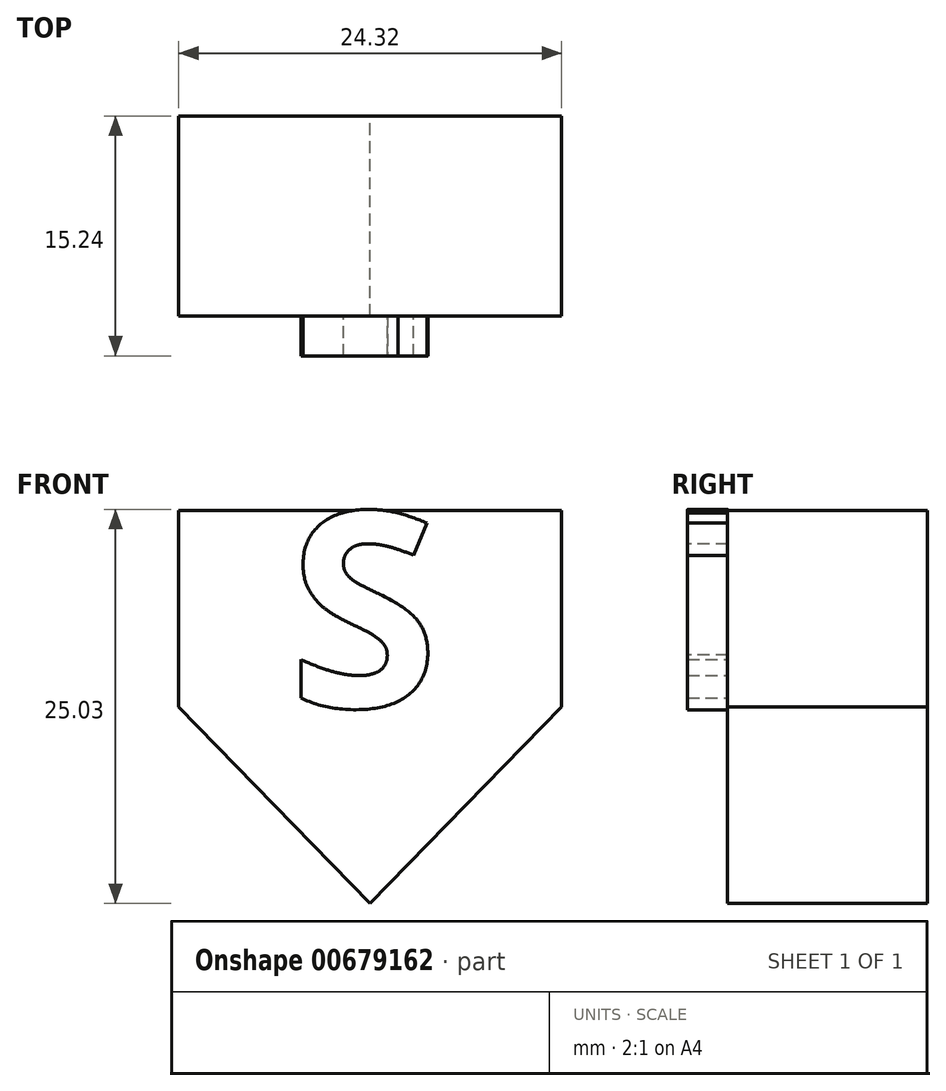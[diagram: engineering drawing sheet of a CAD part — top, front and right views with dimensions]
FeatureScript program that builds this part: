
annotation { "Feature Type Name" : "Feature", "Feature Type Description" : "" }
export const myFeature = defineFeature(function(context is Context, id is Id, definition is map)
    precondition{}
    {
        {
            var Q0;
            Q0=qCreatedBy(makeId("Front.planeOp"),FACE);
            var sketch = newSketch(context, id + "F0", { "sketchPlane" : qUnion([Q0])});
            skLineSegment(sketch, "E0.bottom", {"start": v(12.16, 12.48) * mm, "end": v(-12.16, 12.48) * mm});
            skLineSegment(sketch, "E0.top", {"start": v(12.16, -12.48) * mm, "end": v(-12.16, -12.48) * mm});
            skLineSegment(sketch, "E0.left", {"start": v(12.16, 12.48) * mm, "end": v(12.16, -12.48) * mm});
            skLineSegment(sketch, "E0.right", {"start": v(-12.16, 12.48) * mm, "end": v(-12.16, -12.48) * mm});
            skPoint(sketch, "E0.middle", {"position": v(0, 0) * mm});
            skLineSegment(sketch, "E1", {"start": v(-12.16, 0) * mm, "end": v(0, -12.48) * mm});
            skLineSegment(sketch, "E2", {"start": v(12.16, 0) * mm, "end": v(0, -12.48) * mm});
            skSolve(sketch);
        }
        {
            var Q0;
            {var subQ2=sQuery(id+"F0.wireOp",EDGE,"E0.bottom");Q0=makeQuery(id+"F0.imprint","IMPRINT",FACE,{"disambiguationData":[TD([[makeQuery(id+"F0.imprint","IMPRINT",EDGE,{"derivedFrom":subQ2}),1.0]])]});}
            extrude(context, id + "F1", {"entities" : qUnion([Q0]), "depth" : 12.7 * mm, "offsetDistance" : 25.4 * mm});
        }
        {
            var Q0;
            Q0=makeQuery(id+"F1.opExtrude","CAP_FACE",FACE,{"disambiguationData":[OSD([sQuery(id+"F0.wireOp",EDGE,"E0.bottom"),sQuery(id+"F0.wireOp",EDGE,"E0.left"),sQuery(id+"F0.wireOp",EDGE,"E0.right"),sQuery(id+"F0.wireOp",EDGE,"E1"),sQuery(id+"F0.wireOp",EDGE,"E2")])],"isStart":false});
            var sketch = newSketch(context, id + "F2", { "sketchPlane" : qUnion([Q0])});
            skText(sketch, "E3", { "text": "S", "fontName": "OpenSans-Bold.ttf"});
            const initialGuessF2  = {"E3": [-0.0052, 0, 1, 0, 0.01248]};
            skSetInitialGuess(sketch, initialGuessF2);
            skSolve(sketch);
        }
        {
            var Q0;
            Q0 = qSketchRegion(id + "F2", true);
            extrude(context, id + "F3", {"entities" : qUnion([Q0]), "operationType" : NewBodyOperationType.ADD, "depth" : 2.54 * mm, "offsetDistance" : 25.4 * mm});
        }
    });
